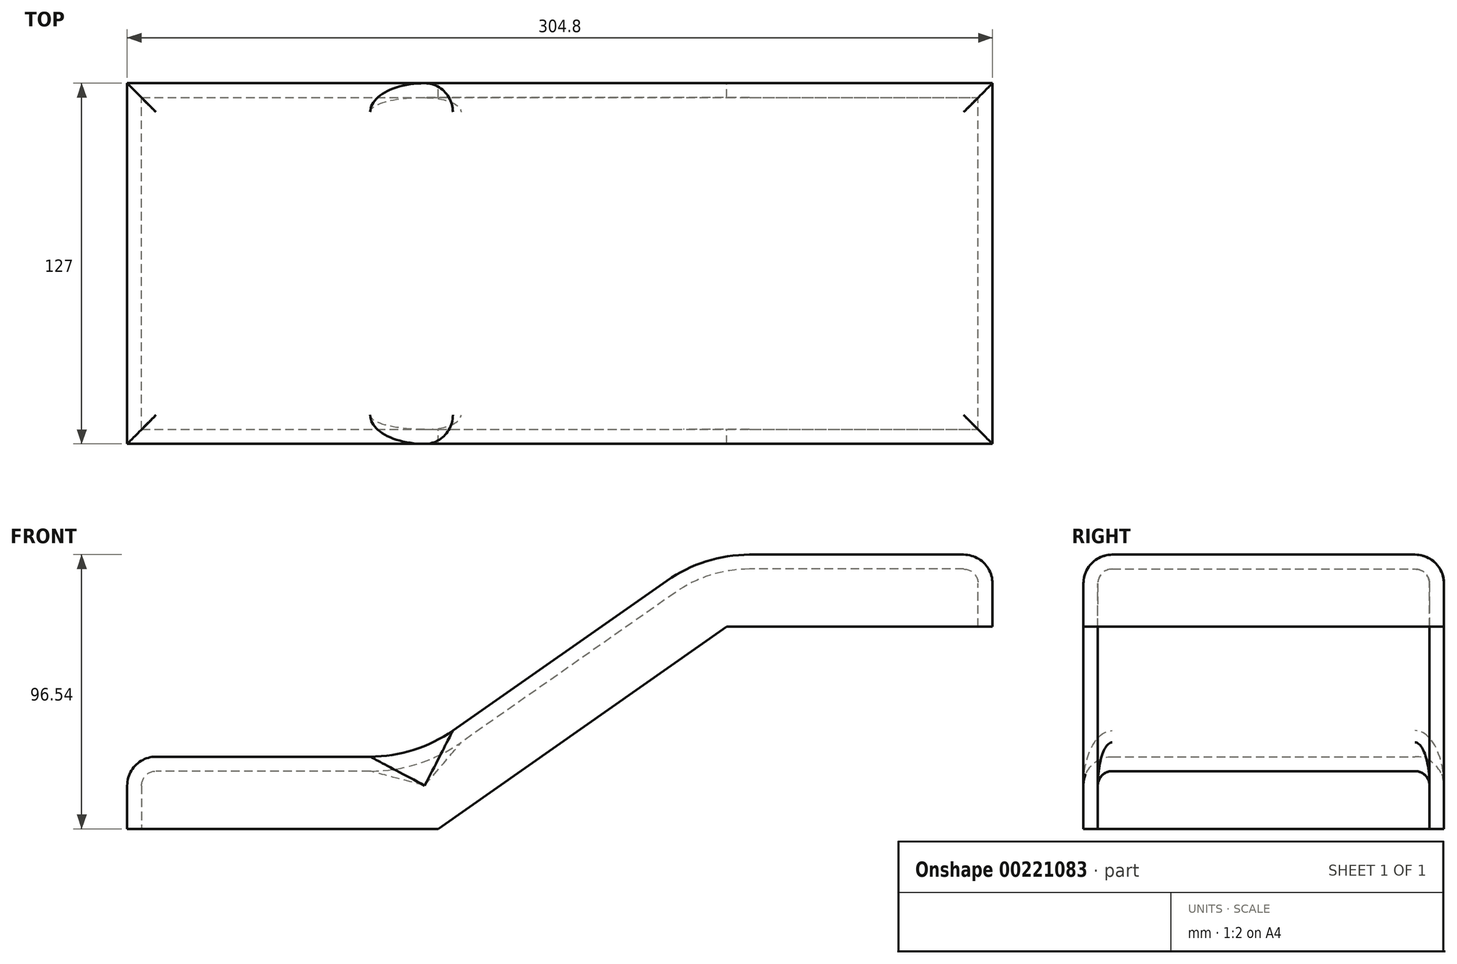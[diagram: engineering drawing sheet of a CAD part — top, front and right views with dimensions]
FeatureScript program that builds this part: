
annotation { "Feature Type Name" : "Feature", "Feature Type Description" : "" }
export const myFeature = defineFeature(function(context is Context, id is Id, definition is map)
    precondition{}
    {
        {
            var Q0;
            Q0=qCreatedBy(makeId("Front.planeOp"),FACE);
            var sketch = newSketch(context, id + "F0", { "sketchPlane" : qUnion([Q0])});
            skLineSegment(sketch, "E0", {"start": v(-152.4, 0) * mm, "end": v(-42.8, 0) * mm});
            skLineSegment(sketch, "E1", {"start": v(-42.8, 0) * mm, "end": v(58.8, 71.14) * mm});
            skLineSegment(sketch, "E2", {"start": v(58.8, 71.14) * mm, "end": v(152.4, 71.14) * mm});
            skLineSegment(sketch, "E3", {"start": v(152.4, 71.14) * mm, "end": v(152.4, 96.54) * mm});
            skLineSegment(sketch, "E4", {"start": v(152.4, 96.54) * mm, "end": v(50.8, 96.54) * mm});
            skLineSegment(sketch, "E5", {"start": v(50.8, 96.54) * mm, "end": v(-50.8, 25.4) * mm});
            skLineSegment(sketch, "E6", {"start": v(-50.8, 25.4) * mm, "end": v(-152.4, 25.4) * mm});
            skLineSegment(sketch, "E7", {"start": v(-152.4, 25.4) * mm, "end": v(-152.4, 0) * mm});
            skSolve(sketch);
        }
        {
            var Q0;
            Q0=makeQuery(id+"F0.imprint","IMPRINT",FACE,{"disambiguationData":[TD([[makeQuery(id+"F0.imprint","IMPRINT",EDGE,{"derivedFrom":sQuery(id+"F0.wireOp",EDGE,"E0")}),1.0]])]});
            extrude(context, id + "F1", {"entities" : qUnion([Q0]), "depth" : 127 * mm});
        }
        {
            var Q0;
            Q0=makeQuery(id+"F1.opExtrude","CAP_EDGE",EDGE,{"disambiguationData":[OSD([sQuery(id+"F0.wireOp",EDGE,"E6")])],"isStart":true});
            var Q1;
            Q1=makeQuery(id+"F1.opExtrude","CAP_EDGE",EDGE,{"disambiguationData":[OSD([sQuery(id+"F0.wireOp",EDGE,"E5")])],"isStart":true});
            var Q2;
            Q2=makeQuery(id+"F1.opExtrude","CAP_EDGE",EDGE,{"disambiguationData":[OSD([sQuery(id+"F0.wireOp",EDGE,"E4")])],"isStart":true});
            var Q3;
            Q3=makeQuery(id+"F1.opExtrude","SWEPT_EDGE",EDGE,{"disambiguationData":[OSD([sQuery(id+"F0.wireOp",EDGE,"E3"),sQuery(id+"F0.wireOp",EDGE,"E4")])]});
            var Q4;
            Q4=makeQuery(id+"F1.opExtrude","SWEPT_EDGE",EDGE,{"disambiguationData":[OSD([sQuery(id+"F0.wireOp",EDGE,"E6"),sQuery(id+"F0.wireOp",EDGE,"E7")])]});
            var Q5;
            Q5=makeQuery(id+"F1.opExtrude","CAP_EDGE",EDGE,{"disambiguationData":[OSD([sQuery(id+"F0.wireOp",EDGE,"E6")])],"isStart":false});
            var Q6;
            Q6=makeQuery(id+"F1.opExtrude","CAP_EDGE",EDGE,{"disambiguationData":[OSD([sQuery(id+"F0.wireOp",EDGE,"E5")])],"isStart":false});
            var Q7;
            Q7=makeQuery(id+"F1.opExtrude","CAP_EDGE",EDGE,{"disambiguationData":[OSD([sQuery(id+"F0.wireOp",EDGE,"E4")])],"isStart":false});
            fillet(context, id + "F2", {"entities" : qUnion([Q0, Q1, Q2, Q3, Q4, Q5, Q6, Q7]), "radius" : 10.16 * mm, "tangentPropagation" : true, "allowEdgeOverflow" : false});
        }
        {
            var Q0;
            Q0=makeQuery(id+"F1.opExtrude","SWEPT_EDGE",EDGE,{"disambiguationData":[OSD([sQuery(id+"F0.wireOp",EDGE,"E4"),sQuery(id+"F0.wireOp",EDGE,"E5")])]});
            var Q1;
            Q1=makeQuery(id+"F1.opExtrude","SWEPT_EDGE",EDGE,{"disambiguationData":[OSD([sQuery(id+"F0.wireOp",EDGE,"E5"),sQuery(id+"F0.wireOp",EDGE,"E6")])]});
            fillet(context, id + "F3", {"entities" : qUnion([Q0, Q1]), "radius" : 50.8 * mm, "tangentPropagation" : true, "allowEdgeOverflow" : false});
        }
        {
            var Q0;
            Q0=makeQuery(id+"F1.opExtrude","SWEPT_FACE",FACE,{"disambiguationData":[OSD([sQuery(id+"F0.wireOp",EDGE,"E2")])]});
            var Q1;
            Q1=makeQuery(id+"F1.opExtrude","SWEPT_FACE",FACE,{"disambiguationData":[OSD([sQuery(id+"F0.wireOp",EDGE,"E1")])]});
            var Q2;
            Q2=makeQuery(id+"F1.opExtrude","SWEPT_FACE",FACE,{"disambiguationData":[OSD([sQuery(id+"F0.wireOp",EDGE,"E0")])]});
            shell(context, id + "F4", {"entities" : qUnion([Q0, Q1, Q2]), "thickness" : 5.08 * mm});
        }
    });
